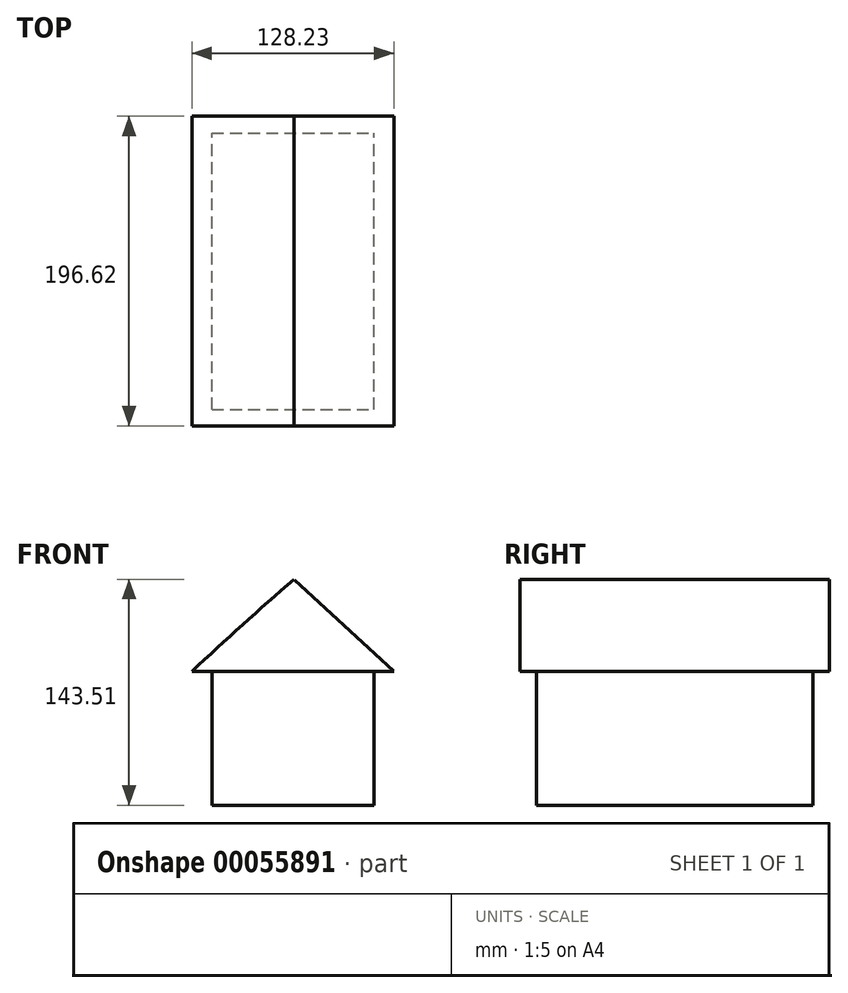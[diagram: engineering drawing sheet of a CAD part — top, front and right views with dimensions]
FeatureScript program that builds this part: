
annotation { "Feature Type Name" : "Feature", "Feature Type Description" : "" }
export const myFeature = defineFeature(function(context is Context, id is Id, definition is map)
    precondition{}
    {
        {
            var Q0;
            Q0=qCreatedBy(makeId("Front.planeOp"),FACE);
            var sketch = newSketch(context, id + "F0", { "sketchPlane" : qUnion([Q0])});
            skLineSegment(sketch, "E0.bottom", {"start": v(-65.2, -76.61) * mm, "end": v(37.62, -76.61) * mm});
            skLineSegment(sketch, "E0.top", {"start": v(-65.2, 8.48) * mm, "end": v(37.62, 8.48) * mm});
            skLineSegment(sketch, "E0.left", {"start": v(-65.2, -76.61) * mm, "end": v(-65.2, 8.48) * mm});
            skLineSegment(sketch, "E0.right", {"start": v(37.62, -76.61) * mm, "end": v(37.62, 8.48) * mm});
            skSolve(sketch);
        }
        {
            var Q0;
            Q0=qCreatedBy(makeId("Front.planeOp"),FACE);
            var sketch = newSketch(context, id + "F1", { "sketchPlane" : qUnion([Q0])});
            skArc(sketch, "E1", {"start": v(-13.18, 66.9) * mm, "mid": v(-45.79, 37.96) * mm, "end": v(-77.9, 8.48) * mm});
            skArc(sketch, "E2", {"start": v(-13.18, 66.9) * mm, "mid": v(18.56, 37.67) * mm, "end": v(50.32, 8.48) * mm});
            skLineSegment(sketch, "E3", {"start": v(-77.9, 8.48) * mm, "end": v(50.32, 8.48) * mm});
            skLineSegment(sketch, "E4", {"start": v(-13.18, 66.9) * mm, "end": v(-13.18, -76.61) * mm, "construction": true});
            skSolve(sketch);
        }
        {
            var Q0;
            Q0=makeQuery(id+"F0.imprint","IMPRINT",FACE,{"disambiguationData":[TD([[makeQuery(id+"F0.imprint","IMPRINT",EDGE,{"derivedFrom":sQuery(id+"F0.wireOp",EDGE,"E0.bottom")}),1.0]])]});
            extrude(context, id + "F2", {"entities" : qUnion([Q0]), "depth" : 175.62 * mm});
        }
        {
            var Q0;
            Q0=makeQuery(id+"F1.imprint","IMPRINT",FACE,{"disambiguationData":[TD([[makeQuery(id+"F1.imprint","IMPRINT",EDGE,{"derivedFrom":sQuery(id+"F1.wireOp",EDGE,"E1")}),1.0]])]});
            extrude(context, id + "F3", {"entities" : qUnion([Q0]), "operationType" : NewBodyOperationType.ADD, "depth" : 186.04 * mm, "hasSecondDirection" : true, "secondDirectionOppositeDirection" : true, "secondDirectionDepth" : 10.58 * mm});
        }
        {
            var Q0;
            Q0=makeQuery(id+"F0.imprint","IMPRINT",FACE,{"disambiguationData":[TD([[makeQuery(id+"F0.imprint","IMPRINT",EDGE,{"derivedFrom":sQuery(id+"F0.wireOp",EDGE,"E0.bottom")}),1.0]])]});
            extrude(context, id + "F4", {"entities" : qUnion([Q0]), "operationType" : NewBodyOperationType.ADD, "depth" : 63.5 * mm});
        }
    });
